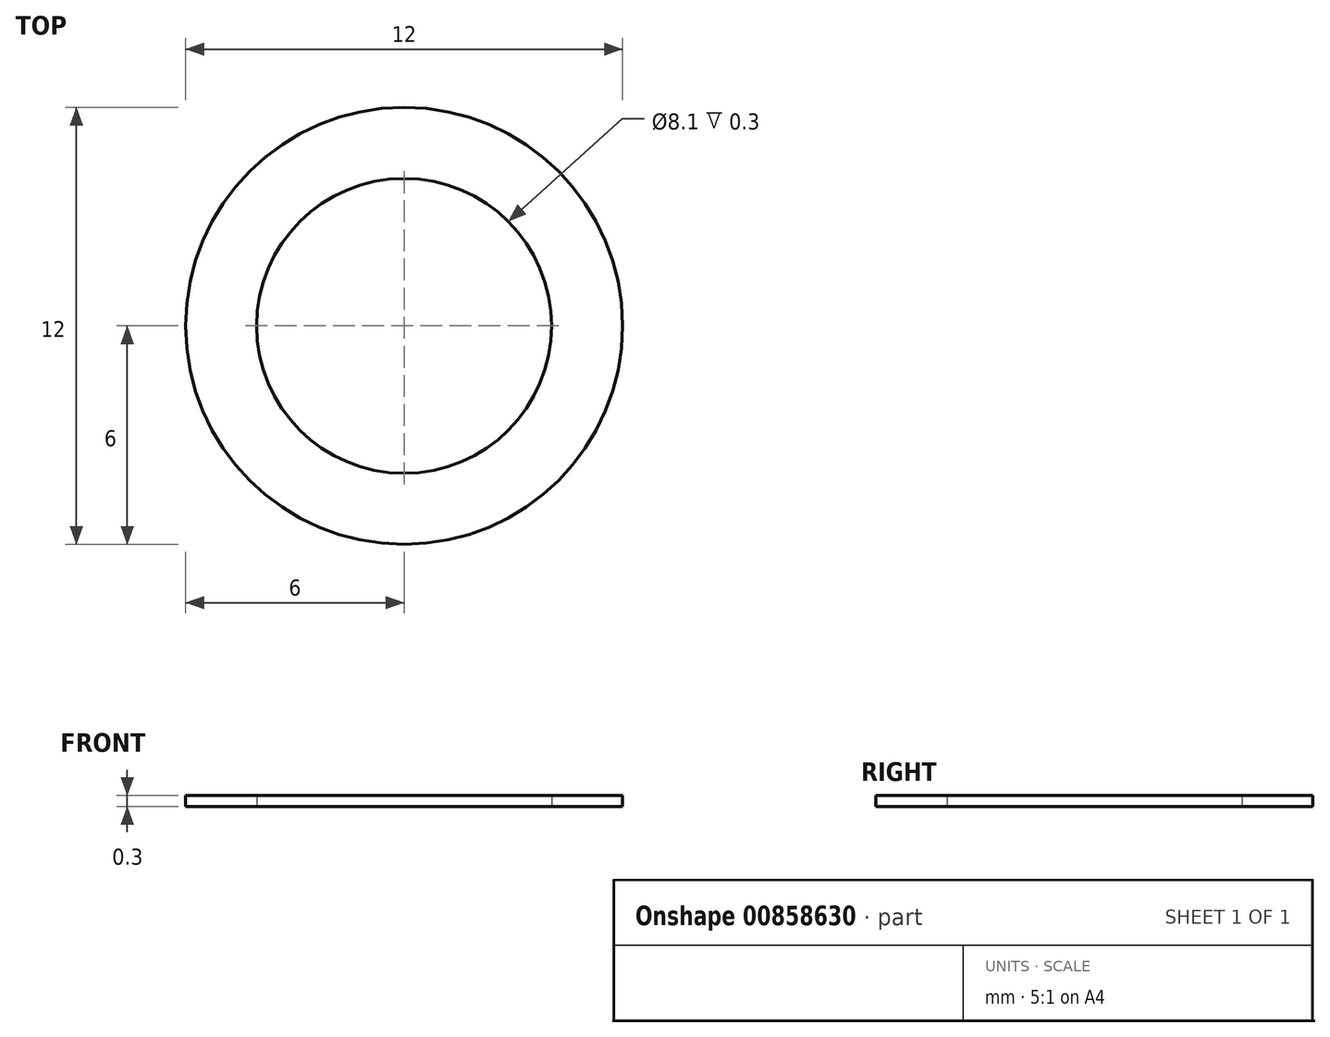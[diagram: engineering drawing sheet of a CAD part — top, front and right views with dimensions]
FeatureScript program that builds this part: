
annotation { "Feature Type Name" : "Feature", "Feature Type Description" : "" }
export const myFeature = defineFeature(function(context is Context, id is Id, definition is map)
    precondition{}
    {
        {
            var Q0;
            Q0=qCreatedBy(makeId("Top.planeOp"),FACE);
            var sketch = newSketch(context, id + "F0", { "sketchPlane" : qUnion([Q0])});
            skCircle(sketch, "E0", {"center": v(0, 0) * mm, "radius": 4.05 * mm});
            skCircle(sketch, "E1", {"center": v(0, 0) * mm, "radius": 6 * mm});
            skSolve(sketch);
        }
        {
            var Q0;
            Q0=makeQuery(id+"F0.imprint","IMPRINT",FACE,{"disambiguationData":[TD([[makeQuery(id+"F0.imprint","IMPRINT",EDGE,{"derivedFrom":sQuery(id+"F0.wireOp",EDGE,"E0")}),-1.0]])]});
            extrude(context, id + "F1", {"entities" : qUnion([Q0]), "depth" : .3 * mm, "offsetDistance" : 25 * mm});
        }
    });
